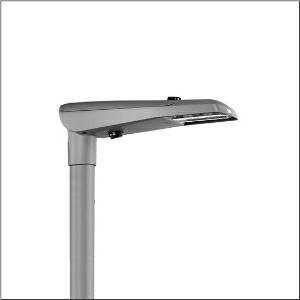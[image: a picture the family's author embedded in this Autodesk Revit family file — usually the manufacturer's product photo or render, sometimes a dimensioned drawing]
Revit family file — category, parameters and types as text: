
# Revit family: streetlight_sl_11_iq_micro___st1_2a_5xc1ac1y08ce_2333
name_source: partatom
category: Lighting Fixtures
units: mm (PartAtom-declared; Revit-internal decimal feet)

## family parameters
Cut with Voids When Loaded = No
Host = Face
Light Source = No
Part Type = Normal
Room Calculation Point = No
Round Connector Dimension = Use Diameter
Shared = No

## types (1)
- --- (1 x LED, 1600 lm, 14 W, 2200K)
    Apparent Load = 14 VA
    CIE Flux Codes = 33 71 96 100 100
    Color Rendering = 70
    Color Temperature = 2200K
    Default Elevation = 1800 mm
    Description = Streetlight SL 11 iQ micro, mast luminaire, primary light control with 3 zone facetted reflector, of plastic, silver coated, highly specular, primary optical cover: cover, of PMMA, transparent, light distribution: ST1.2a, light emission: direct distribution, primary light characteristic: asymmetric, installation type: post-top, side-entry, lamps: LED, High Power LED, rated values: 1.880lm | 13,8W | 136,2lm/W (begin service life); end service life: 1.880lm | 14W; at 50% lumin. flux: 940lm | 7,5W | 125,3lm/W, colour temperature: 2200/2700/3000/4000K, colour rendering: CRI > 70, light colour: 722/727/730/740, light setting 1 begin service life: 100% | 1.880lm | 13,8W | 136,2lm/W | 3.000K, light setting 1 end service life: 14W, further light settings possible, control: pre-setting: logarithmic dimming characteristic, Street-Remote, Auto-Match, Temp-Guard, Lumen-Switch, Night-Set, Smart-Wire, Light-Fading, Desk-Remote (wireless, voltage-free reading and setting of iQ features in the workshop via application-optimized NFC function/RFID function), optimised constant luminous flux control (CLO 2.0), with cable H07RN-F 3x 1.5mm², mains connection: 220..240V, AC, 50/60Hz, connection cable pre-assembled, cable length: 5,5m, luminaire housing, of diecast aluminium, powder-coated, SITECO metallic grey (DB 702S), please order mast flange separately, inclination adjustable without tools: 0°, 5°, 10°, 15° (post-top) | 0°, -5°, -10°, -15° (side-entry), sealing non-destructively replaceable, multi-level sealing system, length: 600mm, width: 174mm, height: 116mm, mast flange for spigot size: 42mm (side-entry): 5XC10008XM4, 60/48mm (side-entry/post-top): 5XC10108XM2, 76/60mm (side-entry/post-top): 5XC10108XM1, equipment: standard, Smart Interface below and above, protection rating (complete): IP66, insulation class (complete): insulation class II (safety insulation), certification: CE, ENEC, ENEC+, VDE, UKCA, impact resistance: IK10, permissible operating ambient temperature for outdoor applications: -25..+50°C, standard-compliant lighting for roads and squares, Environmental Product Declaration (EPD) tested and certified by an independent institute, packaging unit: 1 piece

Light Distribution: ST1.2a
    Height = 116 mm
    Lamp = 1 x LED
    Lamp Light Flux = 1600 lm
    Lamp Power = 14 W
    Lamp count = 1
    Length = 600 mm
    Luminous efficacy = 114 lm/W
    Manufacturer = Siteco
    ModVariant = No
    Model = 5XC1AC1Y08CE
    Number of Poles = 1
    OnlyDefault = Yes
    Power Factor = 1
    Product Name = Streetlight SL 11 iQ micro | ST1.2a
    Product group = mast luminaire | pylon top
    ProductGroupID = 6100
    Protection Class = Protection class II
    Protection Degree = IP 66
    RLX_Detail_Level = 1
    RLX_Emergency_Light_Flux = 0 lm
    RLX_Emergency_Type = 0
    RLX_Emergency_Type_DB = No
    RlxData = <blob elided: 59193 chars, md5=63eac401>
    Socket = socket
    Standby Power = 0 W
    System Light Flux = 1600 lm
    System Power = 14 W
    Type Comments = individual setting: luminous flux: 100 % | dim-lin: 254 | 369 mA
    Type Image = l_1005956.jpg
    URL = http://relux.com
    VarID = @adj_042193
    Voltage = 0 V
    Weight = 0.00 kg
    Width = 174 mm

## geometry (parser evidence)
native form markers: Blend x4, Sweep x11
no freeform markers — native parametric forms only
